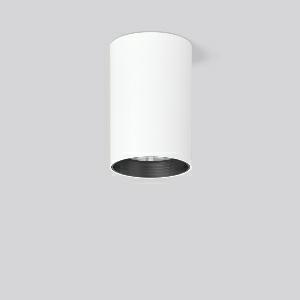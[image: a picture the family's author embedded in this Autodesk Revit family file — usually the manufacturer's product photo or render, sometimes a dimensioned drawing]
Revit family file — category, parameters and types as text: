
# Revit family: heledon_maxi_a_931228_002_76_45e0
name_source: partatom
category: Lighting Fixtures
units: mm (PartAtom-declared; Revit-internal decimal feet)

## family parameters
Cut with Voids When Loaded = No
Host = Face
Light Source = No
Part Type = Normal
Room Calculation Point = No
Round Connector Dimension = Use Diameter
Shared = No

## types (1)
- HELEDON maxi A (1 x LED Modul 930, 3500 lm, 3000)
    Apparent Load = 35 VA
    Approval mark = CE
    CIE Flux Codes = 96 100 100 100 100
    Color Rendering = 90
    Color Temperature = 3000
    Default Elevation = 1800 mm
    Description = Series: HELEDON maxi
Cylindrical surface-mounted downlight. Housing: die-cast aluminium, powder-coated. Internal ceiling frame polycarbonate with bayonet mounting. Black plastic ring and recessed LED to prevent glare from the side. Optical assembly with lens made of plastic (polycarbonate) for the best homogeneous light distribution - can be changed without tools. Best colour rendering index Ra>90. Suitable for Ceiling mounting. Easy installation with a separate ceiling frame with bayonet mounting and plug connection. Driver integrated. Connected via plug-in connector. High quality converter without flickering and stroboscopic effect. The following accessories can be mounted without use of tools: interchangeable lenses, decorative glasses, honeycomb louvre, clear and frosted diffusers, white interchangeable plastic ring. 
Colour: traffic white, matt (RAL 9016)
Diameter: 123 mm
Height: 183 mm
Lamp: LED
Socket: without socket
Colour temperature: 3000K
Colour rendering index (CRI): 92
System power: 35 W
Rated luminous flux: 3500 lm
Luminous efficiency: 100 lm/W
Control gear: Converter, dimmable, DALI
Protection class: I
Type of protection: IP 20
    Height = 183 mm
    Lamp = 1 x LED Modul 930
    Lamp Light Flux = 3500 lm
    Lamp count = 1
    Length = 123 mm
    Lifetime = 50000 h
    Luminous efficacy = 100 lm/W
    Manufacturer = RZB
    ModVariant = No
    Model = 931228.002.76
    Mounting Place = Ceiling
    Mounting Type = Surface mounted
    Number of Poles = 1
    OnlyDefault = Yes
    Power Factor = 1
    Product Name = HELEDON maxi A
    Product group = Surface mounted downlights
    ProductGroupID = 302
    Protection Class = Protection class I
    Protection Degree = IP 20
    RLX_Detail_Level = 1
    RLX_Emergency_Light_Flux = 0 lm
    RLX_Emergency_Type = 0
    RLX_Emergency_Type_DB = No
    RlxData = <blob elided: 96173 chars, md5=0c4d301c>
    Socket = socket
    Standby Power = 0 W
    System Light Flux = 3500 lm
    System Power = 35 W
    Type Comments = Product without accessories
    Type Image = 931193.002.jpg
    URL = http://relux.com
    VarID = ---
    Voltage = 230 V
    Voltage Range = 220-240 V
    Weight = 0.00 kg
    Width = 0 mm  [stored 0 ft]

note: [stored X ft] marks values corroborated as IEEE doubles in the binary element streams (Revit-internal decimal feet)

## geometry (parser evidence)
native form markers: Blend x4, Sweep x10
no freeform markers — native parametric forms only
